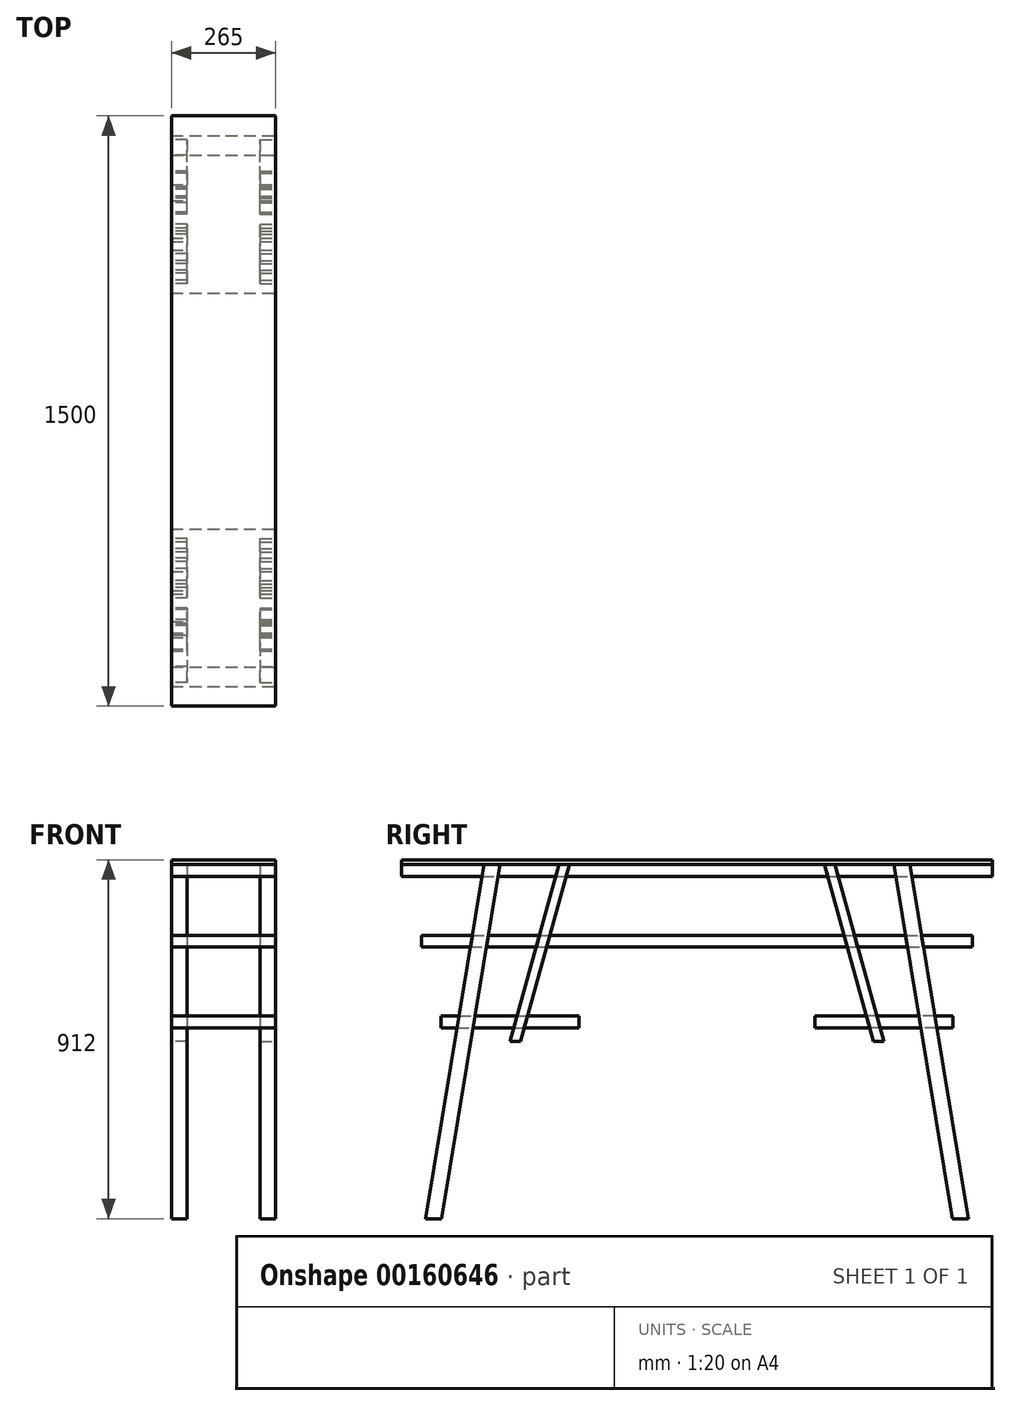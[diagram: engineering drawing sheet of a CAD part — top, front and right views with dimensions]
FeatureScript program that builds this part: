
annotation { "Feature Type Name" : "Feature", "Feature Type Description" : "" }
export const myFeature = defineFeature(function(context is Context, id is Id, definition is map)
    precondition{}
    {
        {
            var Q0;
            Q0=qCreatedBy(makeId("Right.planeOp"),FACE);
            var sketch = newSketch(context, id + "F0", { "sketchPlane" : qUnion([Q0])});
            skLineSegment(sketch, "E0.bottom", {"start": v(0, 0) * mm, "end": v(1500, 0) * mm, "construction": true});
            skLineSegment(sketch, "E0.top", {"start": v(0, 900) * mm, "end": v(1500, 900) * mm, "construction": true});
            skLineSegment(sketch, "E0.left", {"start": v(0, 0) * mm, "end": v(0, 900) * mm, "construction": true});
            skLineSegment(sketch, "E0.right", {"start": v(1500, 0) * mm, "end": v(1500, 900) * mm, "construction": true});
            skLineSegment(sketch, "E1.bottom", {"start": v(0, 900) * mm, "end": v(1500, 900) * mm});
            skLineSegment(sketch, "E1.top", {"start": v(0, 870) * mm, "end": v(1500, 870) * mm});
            skLineSegment(sketch, "E1.left", {"start": v(0, 900) * mm, "end": v(0, 870) * mm});
            skLineSegment(sketch, "E1.right", {"start": v(1500, 900) * mm, "end": v(1500, 870) * mm});
            skLineSegment(sketch, "E2.bottom", {"start": v(50, 720) * mm, "end": v(1450, 720) * mm});
            skLineSegment(sketch, "E2.top", {"start": v(50, 690) * mm, "end": v(1450, 690) * mm});
            skLineSegment(sketch, "E2.left", {"start": v(50, 720) * mm, "end": v(50, 690) * mm});
            skLineSegment(sketch, "E2.right", {"start": v(1450, 720) * mm, "end": v(1450, 690) * mm});
            skLineSegment(sketch, "E3", {"start": v(250, 900) * mm, "end": v(250, 0) * mm, "construction": true});
            skLineSegment(sketch, "E4", {"start": v(250, 900) * mm, "end": v(100.55, 0) * mm});
            skLineSegment(sketch, "E5", {"start": v(209.45, 900) * mm, "end": v(60, 0) * mm});
            skLineSegment(sketch, "E6", {"start": v(60, 0) * mm, "end": v(100.55, 0) * mm});
            skLineSegment(sketch, "E7.MirrorCS", {"start": v(1250, 900) * mm, "end": v(1399.45, 0) * mm});
            skLineSegment(sketch, "E8.MirrorCS", {"start": v(1290.55, 900) * mm, "end": v(1440, 0) * mm});
            skLineSegment(sketch, "E9.MirrorCS", {"start": v(1440, 0) * mm, "end": v(1399.45, 0) * mm});
            skLineSegment(sketch, "E10", {"start": v(400, 900) * mm, "end": v(275.27, 450) * mm});
            skLineSegment(sketch, "E11", {"start": v(275.27, 450) * mm, "end": v(301.22, 450) * mm});
            skLineSegment(sketch, "E12", {"start": v(301.22, 450) * mm, "end": v(425.94, 900) * mm});
            skLineSegment(sketch, "E13.bottom", {"start": v(100, 515) * mm, "end": v(450, 515) * mm});
            skLineSegment(sketch, "E13.top", {"start": v(100, 485) * mm, "end": v(450, 485) * mm});
            skLineSegment(sketch, "E13.left", {"start": v(100, 515) * mm, "end": v(100, 485) * mm});
            skLineSegment(sketch, "E13.right", {"start": v(450, 515) * mm, "end": v(450, 485) * mm});
            skLineSegment(sketch, "E14.MirrorCS", {"start": v(1050, 515) * mm, "end": v(1050, 485) * mm});
            skLineSegment(sketch, "E15.MirrorCS", {"start": v(1400, 515) * mm, "end": v(1400, 485) * mm});
            skLineSegment(sketch, "E16.MirrorCS", {"start": v(1224.73, 450) * mm, "end": v(1198.78, 450) * mm});
            skLineSegment(sketch, "E17.MirrorCS", {"start": v(1400, 515) * mm, "end": v(1050, 515) * mm});
            skLineSegment(sketch, "E18.MirrorCS", {"start": v(1400, 485) * mm, "end": v(1050, 485) * mm});
            skLineSegment(sketch, "E19.MirrorCS", {"start": v(1198.78, 450) * mm, "end": v(1074.06, 900) * mm});
            skLineSegment(sketch, "E20.MirrorCS", {"start": v(1100, 900) * mm, "end": v(1224.73, 450) * mm});
            skLineSegment(sketch, "E21", {"start": v(750, 870) * mm, "end": v(750, 384.96) * mm, "construction": true});
            skPoint(sketch, "E22.orphan", {"position": v(1100, 900) * mm});
            skLineSegment(sketch, "E23", {"start": v(275.27, 450) * mm, "end": v(175.27, 450) * mm, "construction": true});
            skSolve(sketch);
        }
        {
            var Q0;
            {var subQ0=sQuery(id+"F0.wireOp",EDGE,"E1.left");Q0=makeQuery(id+"F0.imprint","IMPRINT",FACE,{"disambiguationData":[TD([[makeQuery(id+"F0.imprint","IMPRINT",EDGE,{"derivedFrom":subQ0}),1.0]])]});}
            var Q1;
            {var subQ0=sQuery(id+"F0.wireOp",EDGE,"E4");var subQ1=sQuery(id+"F0.wireOp",EDGE,"E1.bottom");var subQ2=makeQuery(id+"F0.imprint","INTERSECT",VERTEX,{"derivedFrom":[subQ1,subQ0]});Q1=makeQuery(id+"F0.imprint","IMPRINT",FACE,{"disambiguationData":[TD([[makeQuery(id+"F0.imprint","IMPRINT",EDGE,{"disambiguationData":[TD([[subQ2,1.0]])],"derivedFrom":subQ1}),-1.0]])]});}
            var Q2;
            {var subQ0=sQuery(id+"F0.wireOp",EDGE,"E1.right");Q2=makeQuery(id+"F0.imprint","IMPRINT",FACE,{"disambiguationData":[TD([[makeQuery(id+"F0.imprint","IMPRINT",EDGE,{"derivedFrom":subQ0}),-1.0]])]});}
            var Q3;
            {var subQ0=sQuery(id+"F0.wireOp",EDGE,"E2.left");Q3=makeQuery(id+"F0.imprint","IMPRINT",FACE,{"disambiguationData":[TD([[makeQuery(id+"F0.imprint","IMPRINT",EDGE,{"derivedFrom":subQ0}),1.0]])]});}
            var Q4;
            {var subQ0=sQuery(id+"F0.wireOp",EDGE,"E5");var subQ1=sQuery(id+"F0.wireOp",EDGE,"E2.bottom");var subQ2=makeQuery(id+"F0.imprint","INTERSECT",VERTEX,{"derivedFrom":[subQ1,subQ0]});Q4=makeQuery(id+"F0.imprint","IMPRINT",FACE,{"disambiguationData":[TD([[makeQuery(id+"F0.imprint","IMPRINT",EDGE,{"disambiguationData":[TD([[subQ2,-1.0]])],"derivedFrom":subQ1}),-1.0]])]});}
            var Q5;
            {var subQ0=sQuery(id+"F0.wireOp",EDGE,"E2.right");Q5=makeQuery(id+"F0.imprint","IMPRINT",FACE,{"disambiguationData":[TD([[makeQuery(id+"F0.imprint","IMPRINT",EDGE,{"derivedFrom":subQ0}),-1.0]])]});}
            var Q6;
            {var subQ0=sQuery(id+"F0.wireOp",EDGE,"E4");var subQ1=sQuery(id+"F0.wireOp",EDGE,"E1.bottom");var subQ2=makeQuery(id+"F0.imprint","INTERSECT",VERTEX,{"derivedFrom":[subQ1,subQ0]});Q6=makeQuery(id+"F0.imprint","IMPRINT",FACE,{"disambiguationData":[TD([[makeQuery(id+"F0.imprint","IMPRINT",EDGE,{"disambiguationData":[TD([[subQ2,-1.0]])],"derivedFrom":subQ1}),-1.0]])]});}
            var Q7;
            {var subQ0=sQuery(id+"F0.wireOp",EDGE,"E7.MirrorCS");var subQ1=sQuery(id+"F0.wireOp",EDGE,"E1.bottom");var subQ2=makeQuery(id+"F0.imprint","INTERSECT",VERTEX,{"derivedFrom":[subQ1,subQ0]});Q7=makeQuery(id+"F0.imprint","IMPRINT",FACE,{"disambiguationData":[TD([[makeQuery(id+"F0.imprint","IMPRINT",EDGE,{"disambiguationData":[TD([[subQ2,-1.0]])],"derivedFrom":subQ1}),-1.0]])]});}
            var Q8;
            {var subQ0=sQuery(id+"F0.wireOp",EDGE,"E4");var subQ1=sQuery(id+"F0.wireOp",EDGE,"E2.bottom");var subQ2=makeQuery(id+"F0.imprint","INTERSECT",VERTEX,{"derivedFrom":[subQ1,subQ0]});Q8=makeQuery(id+"F0.imprint","IMPRINT",FACE,{"disambiguationData":[TD([[makeQuery(id+"F0.imprint","IMPRINT",EDGE,{"disambiguationData":[TD([[subQ2,-1.0]])],"derivedFrom":subQ1}),-1.0]])]});}
            var Q9;
            {var subQ0=sQuery(id+"F0.wireOp",EDGE,"E8.MirrorCS");var subQ1=sQuery(id+"F0.wireOp",EDGE,"E2.bottom");var subQ2=makeQuery(id+"F0.imprint","INTERSECT",VERTEX,{"derivedFrom":[subQ1,subQ0]});Q9=makeQuery(id+"F0.imprint","IMPRINT",FACE,{"disambiguationData":[TD([[makeQuery(id+"F0.imprint","IMPRINT",EDGE,{"disambiguationData":[TD([[subQ2,1.0]])],"derivedFrom":subQ1}),-1.0]])]});}
            var Q10;
            {var subQ0=sQuery(id+"F0.wireOp",EDGE,"E10");var subQ1=sQuery(id+"F0.wireOp",EDGE,"E1.bottom");var subQ2=makeQuery(id+"F0.imprint","INTERSECT",VERTEX,{"derivedFrom":[subQ1,subQ0]});Q10=makeQuery(id+"F0.imprint","IMPRINT",FACE,{"disambiguationData":[TD([[makeQuery(id+"F0.imprint","IMPRINT",EDGE,{"disambiguationData":[TD([[subQ2,-1.0]])],"derivedFrom":subQ1}),-1.0]])]});}
            var Q11;
            {var subQ0=sQuery(id+"F0.wireOp",EDGE,"E12");var subQ1=sQuery(id+"F0.wireOp",EDGE,"E1.bottom");var subQ2=makeQuery(id+"F0.imprint","INTERSECT",VERTEX,{"derivedFrom":[subQ1,subQ0]});Q11=makeQuery(id+"F0.imprint","IMPRINT",FACE,{"disambiguationData":[TD([[makeQuery(id+"F0.imprint","IMPRINT",EDGE,{"disambiguationData":[TD([[subQ2,-1.0]])],"derivedFrom":subQ1}),-1.0]])]});}
            var Q12;
            {var subQ0=sQuery(id+"F0.wireOp",EDGE,"E19.MirrorCS");var subQ1=sQuery(id+"F0.wireOp",EDGE,"E1.bottom");var subQ2=makeQuery(id+"F0.imprint","INTERSECT",VERTEX,{"derivedFrom":[subQ1,subQ0]});Q12=makeQuery(id+"F0.imprint","IMPRINT",FACE,{"disambiguationData":[TD([[makeQuery(id+"F0.imprint","IMPRINT",EDGE,{"disambiguationData":[TD([[subQ2,-1.0]])],"derivedFrom":subQ1}),-1.0]])]});}
            var Q13;
            {var subQ0=sQuery(id+"F0.wireOp",EDGE,"E7.MirrorCS");var subQ1=sQuery(id+"F0.wireOp",EDGE,"E1.bottom");var subQ2=makeQuery(id+"F0.imprint","INTERSECT",VERTEX,{"derivedFrom":[subQ1,subQ0]});Q13=makeQuery(id+"F0.imprint","IMPRINT",FACE,{"disambiguationData":[TD([[makeQuery(id+"F0.imprint","IMPRINT",EDGE,{"disambiguationData":[TD([[subQ2,1.0]])],"derivedFrom":subQ1}),-1.0]])]});}
            var Q14;
            {var subQ0=sQuery(id+"F0.wireOp",EDGE,"E10");var subQ1=sQuery(id+"F0.wireOp",EDGE,"E2.bottom");var subQ2=makeQuery(id+"F0.imprint","INTERSECT",VERTEX,{"derivedFrom":[subQ1,subQ0]});Q14=makeQuery(id+"F0.imprint","IMPRINT",FACE,{"disambiguationData":[TD([[makeQuery(id+"F0.imprint","IMPRINT",EDGE,{"disambiguationData":[TD([[subQ2,-1.0]])],"derivedFrom":subQ1}),-1.0]])]});}
            var Q15;
            {var subQ0=sQuery(id+"F0.wireOp",EDGE,"E12");var subQ1=sQuery(id+"F0.wireOp",EDGE,"E2.bottom");var subQ2=makeQuery(id+"F0.imprint","INTERSECT",VERTEX,{"derivedFrom":[subQ1,subQ0]});Q15=makeQuery(id+"F0.imprint","IMPRINT",FACE,{"disambiguationData":[TD([[makeQuery(id+"F0.imprint","IMPRINT",EDGE,{"disambiguationData":[TD([[subQ2,-1.0]])],"derivedFrom":subQ1}),-1.0]])]});}
            var Q16;
            {var subQ0=sQuery(id+"F0.wireOp",EDGE,"E19.MirrorCS");var subQ1=sQuery(id+"F0.wireOp",EDGE,"E2.bottom");var subQ2=makeQuery(id+"F0.imprint","INTERSECT",VERTEX,{"derivedFrom":[subQ1,subQ0]});Q16=makeQuery(id+"F0.imprint","IMPRINT",FACE,{"disambiguationData":[TD([[makeQuery(id+"F0.imprint","IMPRINT",EDGE,{"disambiguationData":[TD([[subQ2,-1.0]])],"derivedFrom":subQ1}),-1.0]])]});}
            var Q17;
            {var subQ0=sQuery(id+"F0.wireOp",EDGE,"E20.MirrorCS");var subQ1=sQuery(id+"F0.wireOp",EDGE,"E2.bottom");var subQ2=makeQuery(id+"F0.imprint","INTERSECT",VERTEX,{"derivedFrom":[subQ1,subQ0]});Q17=makeQuery(id+"F0.imprint","IMPRINT",FACE,{"disambiguationData":[TD([[makeQuery(id+"F0.imprint","IMPRINT",EDGE,{"disambiguationData":[TD([[subQ2,-1.0]])],"derivedFrom":subQ1}),-1.0]])]});}
            var Q18;
            {var subQ5=sQuery(id+"F0.wireOp",EDGE,"E13.left");Q18=makeQuery(id+"F0.imprint","IMPRINT",FACE,{"disambiguationData":[TD([[makeQuery(id+"F0.imprint","IMPRINT",EDGE,{"derivedFrom":subQ5}),1.0]])]});}
            var Q19;
            {var subQ0=sQuery(id+"F0.wireOp",EDGE,"E13.top");var subQ1=sQuery(id+"F0.wireOp",EDGE,"E4");var subQ2=makeQuery(id+"F0.imprint","INTERSECT",VERTEX,{"derivedFrom":[subQ1,subQ0]});Q19=makeQuery(id+"F0.imprint","IMPRINT",FACE,{"disambiguationData":[TD([[makeQuery(id+"F0.imprint","IMPRINT",EDGE,{"disambiguationData":[TD([[subQ2,1.0]])],"derivedFrom":subQ1}),-1.0]])]});}
            var Q20;
            {var subQ0=sQuery(id+"F0.wireOp",EDGE,"E13.top");var subQ1=sQuery(id+"F0.wireOp",EDGE,"E4");var subQ2=makeQuery(id+"F0.imprint","INTERSECT",VERTEX,{"derivedFrom":[subQ1,subQ0]});Q20=makeQuery(id+"F0.imprint","IMPRINT",FACE,{"disambiguationData":[TD([[makeQuery(id+"F0.imprint","IMPRINT",EDGE,{"disambiguationData":[TD([[subQ2,1.0]])],"derivedFrom":subQ1}),1.0]])]});}
            var Q21;
            {var subQ0=sQuery(id+"F0.wireOp",EDGE,"E13.top");var subQ1=sQuery(id+"F0.wireOp",EDGE,"E10");var subQ2=makeQuery(id+"F0.imprint","INTERSECT",VERTEX,{"derivedFrom":[subQ1,subQ0]});Q21=makeQuery(id+"F0.imprint","IMPRINT",FACE,{"disambiguationData":[TD([[makeQuery(id+"F0.imprint","IMPRINT",EDGE,{"disambiguationData":[TD([[subQ2,1.0]])],"derivedFrom":subQ1}),1.0]])]});}
            var Q22;
            {var subQ5=sQuery(id+"F0.wireOp",EDGE,"E13.right");Q22=makeQuery(id+"F0.imprint","IMPRINT",FACE,{"disambiguationData":[TD([[makeQuery(id+"F0.imprint","IMPRINT",EDGE,{"derivedFrom":subQ5}),-1.0]])]});}
            var Q23;
            {var subQ0=sQuery(id+"F0.wireOp",EDGE,"E14.MirrorCS");Q23=makeQuery(id+"F0.imprint","IMPRINT",FACE,{"disambiguationData":[TD([[makeQuery(id+"F0.imprint","IMPRINT",EDGE,{"derivedFrom":subQ0}),1.0]])]});}
            var Q24;
            {var subQ0=sQuery(id+"F0.wireOp",EDGE,"E19.MirrorCS");var subQ1=sQuery(id+"F0.wireOp",EDGE,"E17.MirrorCS");var subQ2=makeQuery(id+"F0.imprint","INTERSECT",VERTEX,{"derivedFrom":[subQ1,subQ0]});Q24=makeQuery(id+"F0.imprint","IMPRINT",FACE,{"disambiguationData":[TD([[makeQuery(id+"F0.imprint","IMPRINT",EDGE,{"disambiguationData":[TD([[subQ2,1.0]])],"derivedFrom":subQ1}),1.0]])]});}
            var Q25;
            {var subQ0=sQuery(id+"F0.wireOp",EDGE,"E18.MirrorCS");var subQ1=sQuery(id+"F0.wireOp",EDGE,"E7.MirrorCS");var subQ2=makeQuery(id+"F0.imprint","INTERSECT",VERTEX,{"derivedFrom":[subQ1,subQ0]});Q25=makeQuery(id+"F0.imprint","IMPRINT",FACE,{"disambiguationData":[TD([[makeQuery(id+"F0.imprint","IMPRINT",EDGE,{"disambiguationData":[TD([[subQ2,1.0]])],"derivedFrom":subQ1}),-1.0]])]});}
            var Q26;
            {var subQ0=sQuery(id+"F0.wireOp",EDGE,"E18.MirrorCS");var subQ1=sQuery(id+"F0.wireOp",EDGE,"E7.MirrorCS");var subQ2=makeQuery(id+"F0.imprint","INTERSECT",VERTEX,{"derivedFrom":[subQ1,subQ0]});Q26=makeQuery(id+"F0.imprint","IMPRINT",FACE,{"disambiguationData":[TD([[makeQuery(id+"F0.imprint","IMPRINT",EDGE,{"disambiguationData":[TD([[subQ2,1.0]])],"derivedFrom":subQ1}),1.0]])]});}
            var Q27;
            {var subQ5=sQuery(id+"F0.wireOp",EDGE,"E15.MirrorCS");Q27=makeQuery(id+"F0.imprint","IMPRINT",FACE,{"disambiguationData":[TD([[makeQuery(id+"F0.imprint","IMPRINT",EDGE,{"derivedFrom":subQ5}),-1.0]])]});}
            extrude(context, id + "F1", {"entities" : qUnion([Q0, Q1, Q2, Q3, Q4, Q5, Q6, Q7, Q8, Q9, Q10, Q11, Q12, Q13, Q14, Q15, Q16, Q17, Q18, Q19, Q20, Q21, Q22, Q23, Q24, Q25, Q26, Q27]), "oppositeDirection" : true, "depth" : 265 * mm});
        }
        {
            var Q0;
            Q0=makeQuery(id+"F1.opExtrude","CAP_FACE",FACE,{"disambiguationData":[OSD([sQuery(id+"F0.wireOp",EDGE,"E1.bottom"),sQuery(id+"F0.wireOp",EDGE,"E1.top"),sQuery(id+"F0.wireOp",EDGE,"E1.left"),sQuery(id+"F0.wireOp",EDGE,"E1.right")])],"isStart":false});
            var sketch = newSketch(context, id + "F2", { "sketchPlane" : qUnion([Q0])});
            skLineSegment(sketch, "E24.0", {"start": v(-209.45, 900) * mm, "end": v(-60, 0) * mm});
            skLineSegment(sketch, "E25.0", {"start": v(-250, 900) * mm, "end": v(-100.55, 0) * mm});
            skLineSegment(sketch, "E26.0", {"start": v(-1250, 900) * mm, "end": v(-1399.45, 0) * mm});
            skLineSegment(sketch, "E27.0", {"start": v(-1290.55, 900) * mm, "end": v(-1440, 0) * mm});
            skLineSegment(sketch, "E28.0", {"start": v(-1440, 0) * mm, "end": v(-1399.45, 0) * mm});
            skLineSegment(sketch, "E29.0", {"start": v(-60, 0) * mm, "end": v(-100.55, 0) * mm});
            skLineSegment(sketch, "E30.0", {"start": v(0, 900) * mm, "end": v(-1500, 900) * mm});
            skLineSegment(sketch, "E31.0", {"start": v(-301.22, 450) * mm, "end": v(-425.94, 900) * mm});
            skLineSegment(sketch, "E32.0", {"start": v(-275.27, 450) * mm, "end": v(-301.22, 450) * mm});
            skLineSegment(sketch, "E33.0", {"start": v(-400, 900) * mm, "end": v(-275.27, 450) * mm});
            skLineSegment(sketch, "E34.0", {"start": v(-1100, 900) * mm, "end": v(-1224.73, 450) * mm});
            skLineSegment(sketch, "E34.1", {"start": v(-1198.78, 450) * mm, "end": v(-1074.06, 900) * mm});
            skLineSegment(sketch, "E34.2", {"start": v(-1224.73, 450) * mm, "end": v(-1198.78, 450) * mm});
            skLineSegment(sketch, "E35.0", {"start": v(-100, 515) * mm, "end": v(-450, 515) * mm});
            skLineSegment(sketch, "E36.0", {"start": v(-50, 720) * mm, "end": v(-1450, 720) * mm});
            skSolve(sketch);
        }
        {
            var Q0;
            {var subQ0=sQuery(id+"F0.wireOp",EDGE,"E4");var subQ1=sQuery(id+"F0.wireOp",EDGE,"E1.bottom");var subQ2=makeQuery(id+"F0.imprint","INTERSECT",VERTEX,{"derivedFrom":[subQ1,subQ0]});Q0=makeQuery(id+"F0.imprint","IMPRINT",FACE,{"disambiguationData":[TD([[makeQuery(id+"F0.imprint","IMPRINT",EDGE,{"disambiguationData":[TD([[subQ2,1.0]])],"derivedFrom":subQ1}),-1.0]])]});}
            var Q1;
            {var subQ0=sQuery(id+"F0.wireOp",EDGE,"E5");var subQ1=sQuery(id+"F0.wireOp",EDGE,"E2.bottom");var subQ2=makeQuery(id+"F0.imprint","INTERSECT",VERTEX,{"derivedFrom":[subQ1,subQ0]});Q1=makeQuery(id+"F0.imprint","IMPRINT",FACE,{"disambiguationData":[TD([[makeQuery(id+"F0.imprint","IMPRINT",EDGE,{"disambiguationData":[TD([[subQ2,-1.0]])],"derivedFrom":subQ1}),-1.0]])]});}
            var Q2;
            {var subQ0=sQuery(id+"F0.wireOp",EDGE,"E7.MirrorCS");var subQ1=sQuery(id+"F0.wireOp",EDGE,"E1.bottom");var subQ2=makeQuery(id+"F0.imprint","INTERSECT",VERTEX,{"derivedFrom":[subQ1,subQ0]});Q2=makeQuery(id+"F0.imprint","IMPRINT",FACE,{"disambiguationData":[TD([[makeQuery(id+"F0.imprint","IMPRINT",EDGE,{"disambiguationData":[TD([[subQ2,-1.0]])],"derivedFrom":subQ1}),-1.0]])]});}
            var Q3;
            {var subQ0=sQuery(id+"F0.wireOp",EDGE,"E8.MirrorCS");var subQ1=sQuery(id+"F0.wireOp",EDGE,"E2.bottom");var subQ2=makeQuery(id+"F0.imprint","INTERSECT",VERTEX,{"derivedFrom":[subQ1,subQ0]});Q3=makeQuery(id+"F0.imprint","IMPRINT",FACE,{"disambiguationData":[TD([[makeQuery(id+"F0.imprint","IMPRINT",EDGE,{"disambiguationData":[TD([[subQ2,1.0]])],"derivedFrom":subQ1}),-1.0]])]});}
            var Q4;
            {var subQ0=sQuery(id+"F0.wireOp",EDGE,"E10");var subQ1=sQuery(id+"F0.wireOp",EDGE,"E2.bottom");var subQ2=makeQuery(id+"F0.imprint","INTERSECT",VERTEX,{"derivedFrom":[subQ1,subQ0]});Q4=makeQuery(id+"F0.imprint","IMPRINT",FACE,{"disambiguationData":[TD([[makeQuery(id+"F0.imprint","IMPRINT",EDGE,{"disambiguationData":[TD([[subQ2,-1.0]])],"derivedFrom":subQ1}),-1.0]])]});}
            var Q5;
            {var subQ0=sQuery(id+"F0.wireOp",EDGE,"E10");var subQ1=sQuery(id+"F0.wireOp",EDGE,"E1.bottom");var subQ2=makeQuery(id+"F0.imprint","INTERSECT",VERTEX,{"derivedFrom":[subQ1,subQ0]});Q5=makeQuery(id+"F0.imprint","IMPRINT",FACE,{"disambiguationData":[TD([[makeQuery(id+"F0.imprint","IMPRINT",EDGE,{"disambiguationData":[TD([[subQ2,-1.0]])],"derivedFrom":subQ1}),-1.0]])]});}
            var Q6;
            {var subQ0=sQuery(id+"F0.wireOp",EDGE,"E19.MirrorCS");var subQ1=sQuery(id+"F0.wireOp",EDGE,"E1.bottom");var subQ2=makeQuery(id+"F0.imprint","INTERSECT",VERTEX,{"derivedFrom":[subQ1,subQ0]});Q6=makeQuery(id+"F0.imprint","IMPRINT",FACE,{"disambiguationData":[TD([[makeQuery(id+"F0.imprint","IMPRINT",EDGE,{"disambiguationData":[TD([[subQ2,-1.0]])],"derivedFrom":subQ1}),-1.0]])]});}
            var Q7;
            {var subQ0=sQuery(id+"F0.wireOp",EDGE,"E19.MirrorCS");var subQ1=sQuery(id+"F0.wireOp",EDGE,"E2.bottom");var subQ2=makeQuery(id+"F0.imprint","INTERSECT",VERTEX,{"derivedFrom":[subQ1,subQ0]});Q7=makeQuery(id+"F0.imprint","IMPRINT",FACE,{"disambiguationData":[TD([[makeQuery(id+"F0.imprint","IMPRINT",EDGE,{"disambiguationData":[TD([[subQ2,-1.0]])],"derivedFrom":subQ1}),-1.0]])]});}
            var Q8;
            {var subQ0=sQuery(id+"F0.wireOp",EDGE,"E13.top");var subQ1=sQuery(id+"F0.wireOp",EDGE,"E4");var subQ2=makeQuery(id+"F0.imprint","INTERSECT",VERTEX,{"derivedFrom":[subQ1,subQ0]});Q8=makeQuery(id+"F0.imprint","IMPRINT",FACE,{"disambiguationData":[TD([[makeQuery(id+"F0.imprint","IMPRINT",EDGE,{"disambiguationData":[TD([[subQ2,1.0]])],"derivedFrom":subQ1}),-1.0]])]});}
            var Q9;
            {var subQ0=sQuery(id+"F0.wireOp",EDGE,"E13.top");var subQ1=sQuery(id+"F0.wireOp",EDGE,"E10");var subQ2=makeQuery(id+"F0.imprint","INTERSECT",VERTEX,{"derivedFrom":[subQ1,subQ0]});Q9=makeQuery(id+"F0.imprint","IMPRINT",FACE,{"disambiguationData":[TD([[makeQuery(id+"F0.imprint","IMPRINT",EDGE,{"disambiguationData":[TD([[subQ2,1.0]])],"derivedFrom":subQ1}),1.0]])]});}
            var Q10;
            {var subQ0=sQuery(id+"F0.wireOp",EDGE,"E19.MirrorCS");var subQ1=sQuery(id+"F0.wireOp",EDGE,"E17.MirrorCS");var subQ2=makeQuery(id+"F0.imprint","INTERSECT",VERTEX,{"derivedFrom":[subQ1,subQ0]});Q10=makeQuery(id+"F0.imprint","IMPRINT",FACE,{"disambiguationData":[TD([[makeQuery(id+"F0.imprint","IMPRINT",EDGE,{"disambiguationData":[TD([[subQ2,1.0]])],"derivedFrom":subQ1}),1.0]])]});}
            var Q11;
            {var subQ0=sQuery(id+"F0.wireOp",EDGE,"E18.MirrorCS");var subQ1=sQuery(id+"F0.wireOp",EDGE,"E7.MirrorCS");var subQ2=makeQuery(id+"F0.imprint","INTERSECT",VERTEX,{"derivedFrom":[subQ1,subQ0]});Q11=makeQuery(id+"F0.imprint","IMPRINT",FACE,{"disambiguationData":[TD([[makeQuery(id+"F0.imprint","IMPRINT",EDGE,{"disambiguationData":[TD([[subQ2,1.0]])],"derivedFrom":subQ1}),1.0]])]});}
            extrude(context, id + "F3", {"entities" : qUnion([Q0, Q1, Q2, Q3, Q4, Q5, Q6, Q7, Q8, Q9, Q10, Q11]), "operationType" : NewBodyOperationType.REMOVE, "oppositeDirection" : true, "depth" : 40 * mm});
        }
        {
            var Q0;
            {var subQ0=sQuery(id+"F2.wireOp",EDGE,"E30.0");var subQ1=sQuery(id+"F2.wireOp",EDGE,"E26.0");var subQ2=makeQuery(id+"F2.imprint","INTERSECT",VERTEX,{"derivedFrom":[subQ1,subQ0]});Q0=makeQuery(id+"F2.imprint","IMPRINT",FACE,{"disambiguationData":[TD([[makeQuery(id+"F2.imprint","IMPRINT",EDGE,{"disambiguationData":[TD([[subQ2,-1.0]])],"derivedFrom":subQ1}),-1.0]])]});}
            var Q1;
            {var subQ0=sQuery(id+"F2.wireOp",EDGE,"E30.0");var subQ1=sQuery(id+"F2.wireOp",EDGE,"E34.0");var subQ2=makeQuery(id+"F2.imprint","INTERSECT",VERTEX,{"derivedFrom":[subQ1,subQ0]});Q1=makeQuery(id+"F2.imprint","IMPRINT",FACE,{"disambiguationData":[TD([[makeQuery(id+"F2.imprint","IMPRINT",EDGE,{"disambiguationData":[TD([[subQ2,-1.0]])],"derivedFrom":subQ1}),1.0]])]});}
            var Q2;
            {var subQ0=sQuery(id+"F2.wireOp",EDGE,"E30.0");var subQ1=sQuery(id+"F2.wireOp",EDGE,"E31.0");var subQ2=makeQuery(id+"F2.imprint","INTERSECT",VERTEX,{"derivedFrom":[subQ1,subQ0]});Q2=makeQuery(id+"F2.imprint","IMPRINT",FACE,{"disambiguationData":[TD([[makeQuery(id+"F2.imprint","IMPRINT",EDGE,{"disambiguationData":[TD([[subQ2,1.0]])],"derivedFrom":subQ1}),-1.0]])]});}
            var Q3;
            {var subQ0=sQuery(id+"F2.wireOp",EDGE,"E30.0");var subQ1=sQuery(id+"F2.wireOp",EDGE,"E24.0");var subQ2=makeQuery(id+"F2.imprint","INTERSECT",VERTEX,{"derivedFrom":[subQ1,subQ0]});Q3=makeQuery(id+"F2.imprint","IMPRINT",FACE,{"disambiguationData":[TD([[makeQuery(id+"F2.imprint","IMPRINT",EDGE,{"disambiguationData":[TD([[subQ2,-1.0]])],"derivedFrom":subQ1}),-1.0]])]});}
            var Q4;
            {var subQ0=sQuery(id+"F2.wireOp",EDGE,"E28.0");Q4=makeQuery(id+"F2.imprint","IMPRINT",FACE,{"disambiguationData":[TD([[makeQuery(id+"F2.imprint","IMPRINT",EDGE,{"derivedFrom":subQ0}),1.0]])]});}
            var Q5;
            {var subQ0=sQuery(id+"F2.wireOp",EDGE,"E34.2");Q5=makeQuery(id+"F2.imprint","IMPRINT",FACE,{"disambiguationData":[TD([[makeQuery(id+"F2.imprint","IMPRINT",EDGE,{"derivedFrom":subQ0}),1.0]])]});}
            var Q6;
            {var subQ0=sQuery(id+"F2.wireOp",EDGE,"E35.0");var subQ1=sQuery(id+"F2.wireOp",EDGE,"E31.0");var subQ2=makeQuery(id+"F2.imprint","INTERSECT",VERTEX,{"derivedFrom":[subQ1,subQ0]});Q6=makeQuery(id+"F2.imprint","IMPRINT",FACE,{"disambiguationData":[TD([[makeQuery(id+"F2.imprint","IMPRINT",EDGE,{"disambiguationData":[TD([[subQ2,-1.0]])],"derivedFrom":subQ1}),-1.0]])]});}
            var Q7;
            {var subQ0=sQuery(id+"F2.wireOp",EDGE,"E32.0");Q7=makeQuery(id+"F2.imprint","IMPRINT",FACE,{"disambiguationData":[TD([[makeQuery(id+"F2.imprint","IMPRINT",EDGE,{"derivedFrom":subQ0}),-1.0]])]});}
            var Q8;
            {var subQ0=sQuery(id+"F2.wireOp",EDGE,"E36.0");var subQ1=sQuery(id+"F2.wireOp",EDGE,"E24.0");var subQ2=makeQuery(id+"F2.imprint","INTERSECT",VERTEX,{"derivedFrom":[subQ1,subQ0]});Q8=makeQuery(id+"F2.imprint","IMPRINT",FACE,{"disambiguationData":[TD([[makeQuery(id+"F2.imprint","IMPRINT",EDGE,{"disambiguationData":[TD([[subQ2,-1.0]])],"derivedFrom":subQ1}),-1.0]])]});}
            var Q9;
            {var subQ0=sQuery(id+"F2.wireOp",EDGE,"E29.0");Q9=makeQuery(id+"F2.imprint","IMPRINT",FACE,{"disambiguationData":[TD([[makeQuery(id+"F2.imprint","IMPRINT",EDGE,{"derivedFrom":subQ0}),-1.0]])]});}
            extrude(context, id + "F4", {"entities" : qUnion([Q0, Q1, Q2, Q3, Q4, Q5, Q6, Q7, Q8, Q9]), "operationType" : NewBodyOperationType.REMOVE, "oppositeDirection" : true, "depth" : 40 * mm});
        }
        {
            var Q0;
            {var subQ0=sQuery(id+"F0.wireOp",EDGE,"E4");var subQ1=sQuery(id+"F0.wireOp",EDGE,"E1.bottom");var subQ2=makeQuery(id+"F0.imprint","INTERSECT",VERTEX,{"derivedFrom":[subQ1,subQ0]});Q0=makeQuery(id+"F0.imprint","IMPRINT",FACE,{"disambiguationData":[TD([[makeQuery(id+"F0.imprint","IMPRINT",EDGE,{"disambiguationData":[TD([[subQ2,1.0]])],"derivedFrom":subQ1}),-1.0]])]});}
            var Q1;
            {var subQ0=sQuery(id+"F0.wireOp",EDGE,"E5");var subQ1=sQuery(id+"F0.wireOp",EDGE,"E1.top");var subQ2=makeQuery(id+"F0.imprint","INTERSECT",VERTEX,{"derivedFrom":[subQ1,subQ0]});Q1=makeQuery(id+"F0.imprint","IMPRINT",FACE,{"disambiguationData":[TD([[makeQuery(id+"F0.imprint","IMPRINT",EDGE,{"disambiguationData":[TD([[subQ2,-1.0]])],"derivedFrom":subQ1}),-1.0]])]});}
            var Q2;
            {var subQ5=sQuery(id+"F0.wireOp",EDGE,"E6");Q2=makeQuery(id+"F0.imprint","IMPRINT",FACE,{"disambiguationData":[TD([[makeQuery(id+"F0.imprint","IMPRINT",EDGE,{"derivedFrom":subQ5}),1.0]])]});}
            var Q3;
            {var subQ0=sQuery(id+"F0.wireOp",EDGE,"E7.MirrorCS");var subQ1=sQuery(id+"F0.wireOp",EDGE,"E1.bottom");var subQ2=makeQuery(id+"F0.imprint","INTERSECT",VERTEX,{"derivedFrom":[subQ1,subQ0]});Q3=makeQuery(id+"F0.imprint","IMPRINT",FACE,{"disambiguationData":[TD([[makeQuery(id+"F0.imprint","IMPRINT",EDGE,{"disambiguationData":[TD([[subQ2,-1.0]])],"derivedFrom":subQ1}),-1.0]])]});}
            var Q4;
            {var subQ0=sQuery(id+"F0.wireOp",EDGE,"E8.MirrorCS");var subQ1=sQuery(id+"F0.wireOp",EDGE,"E1.top");var subQ2=makeQuery(id+"F0.imprint","INTERSECT",VERTEX,{"derivedFrom":[subQ1,subQ0]});Q4=makeQuery(id+"F0.imprint","IMPRINT",FACE,{"disambiguationData":[TD([[makeQuery(id+"F0.imprint","IMPRINT",EDGE,{"disambiguationData":[TD([[subQ2,1.0]])],"derivedFrom":subQ1}),-1.0]])]});}
            var Q5;
            {var subQ0=sQuery(id+"F0.wireOp",EDGE,"E8.MirrorCS");var subQ1=sQuery(id+"F0.wireOp",EDGE,"E2.bottom");var subQ2=makeQuery(id+"F0.imprint","INTERSECT",VERTEX,{"derivedFrom":[subQ1,subQ0]});Q5=makeQuery(id+"F0.imprint","IMPRINT",FACE,{"disambiguationData":[TD([[makeQuery(id+"F0.imprint","IMPRINT",EDGE,{"disambiguationData":[TD([[subQ2,1.0]])],"derivedFrom":subQ1}),-1.0]])]});}
            var Q6;
            {var subQ5=sQuery(id+"F0.wireOp",EDGE,"E9.MirrorCS");Q6=makeQuery(id+"F0.imprint","IMPRINT",FACE,{"disambiguationData":[TD([[makeQuery(id+"F0.imprint","IMPRINT",EDGE,{"derivedFrom":subQ5}),-1.0]])]});}
            var Q7;
            {var subQ0=sQuery(id+"F0.wireOp",EDGE,"E5");var subQ1=sQuery(id+"F0.wireOp",EDGE,"E2.top");var subQ2=makeQuery(id+"F0.imprint","INTERSECT",VERTEX,{"derivedFrom":[subQ1,subQ0]});Q7=makeQuery(id+"F0.imprint","IMPRINT",FACE,{"disambiguationData":[TD([[makeQuery(id+"F0.imprint","IMPRINT",EDGE,{"disambiguationData":[TD([[subQ2,-1.0]])],"derivedFrom":subQ1}),-1.0]])]});}
            var Q8;
            {var subQ0=sQuery(id+"F0.wireOp",EDGE,"E5");var subQ1=sQuery(id+"F0.wireOp",EDGE,"E2.bottom");var subQ2=makeQuery(id+"F0.imprint","INTERSECT",VERTEX,{"derivedFrom":[subQ1,subQ0]});Q8=makeQuery(id+"F0.imprint","IMPRINT",FACE,{"disambiguationData":[TD([[makeQuery(id+"F0.imprint","IMPRINT",EDGE,{"disambiguationData":[TD([[subQ2,-1.0]])],"derivedFrom":subQ1}),-1.0]])]});}
            var Q9;
            {var subQ0=sQuery(id+"F0.wireOp",EDGE,"E13.top");var subQ1=sQuery(id+"F0.wireOp",EDGE,"E4");var subQ2=makeQuery(id+"F0.imprint","INTERSECT",VERTEX,{"derivedFrom":[subQ1,subQ0]});Q9=makeQuery(id+"F0.imprint","IMPRINT",FACE,{"disambiguationData":[TD([[makeQuery(id+"F0.imprint","IMPRINT",EDGE,{"disambiguationData":[TD([[subQ2,1.0]])],"derivedFrom":subQ1}),-1.0]])]});}
            var Q10;
            {var subQ0=sQuery(id+"F0.wireOp",EDGE,"E8.MirrorCS");var subQ1=sQuery(id+"F0.wireOp",EDGE,"E2.top");var subQ2=makeQuery(id+"F0.imprint","INTERSECT",VERTEX,{"derivedFrom":[subQ1,subQ0]});Q10=makeQuery(id+"F0.imprint","IMPRINT",FACE,{"disambiguationData":[TD([[makeQuery(id+"F0.imprint","IMPRINT",EDGE,{"disambiguationData":[TD([[subQ2,1.0]])],"derivedFrom":subQ1}),-1.0]])]});}
            var Q11;
            {var subQ0=sQuery(id+"F0.wireOp",EDGE,"E18.MirrorCS");var subQ1=sQuery(id+"F0.wireOp",EDGE,"E7.MirrorCS");var subQ2=makeQuery(id+"F0.imprint","INTERSECT",VERTEX,{"derivedFrom":[subQ1,subQ0]});Q11=makeQuery(id+"F0.imprint","IMPRINT",FACE,{"disambiguationData":[TD([[makeQuery(id+"F0.imprint","IMPRINT",EDGE,{"disambiguationData":[TD([[subQ2,1.0]])],"derivedFrom":subQ1}),1.0]])]});}
            var Q12;
            {var subQ0=sQuery(id+"F0.wireOp",EDGE,"E10");var subQ1=sQuery(id+"F0.wireOp",EDGE,"E1.bottom");var subQ2=makeQuery(id+"F0.imprint","INTERSECT",VERTEX,{"derivedFrom":[subQ1,subQ0]});Q12=makeQuery(id+"F0.imprint","IMPRINT",FACE,{"disambiguationData":[TD([[makeQuery(id+"F0.imprint","IMPRINT",EDGE,{"disambiguationData":[TD([[subQ2,-1.0]])],"derivedFrom":subQ1}),-1.0]])]});}
            var Q13;
            {var subQ0=sQuery(id+"F0.wireOp",EDGE,"E10");var subQ1=sQuery(id+"F0.wireOp",EDGE,"E1.top");var subQ2=makeQuery(id+"F0.imprint","INTERSECT",VERTEX,{"derivedFrom":[subQ1,subQ0]});Q13=makeQuery(id+"F0.imprint","IMPRINT",FACE,{"disambiguationData":[TD([[makeQuery(id+"F0.imprint","IMPRINT",EDGE,{"disambiguationData":[TD([[subQ2,-1.0]])],"derivedFrom":subQ1}),-1.0]])]});}
            var Q14;
            {var subQ0=sQuery(id+"F0.wireOp",EDGE,"E10");var subQ1=sQuery(id+"F0.wireOp",EDGE,"E2.bottom");var subQ2=makeQuery(id+"F0.imprint","INTERSECT",VERTEX,{"derivedFrom":[subQ1,subQ0]});Q14=makeQuery(id+"F0.imprint","IMPRINT",FACE,{"disambiguationData":[TD([[makeQuery(id+"F0.imprint","IMPRINT",EDGE,{"disambiguationData":[TD([[subQ2,-1.0]])],"derivedFrom":subQ1}),-1.0]])]});}
            var Q15;
            {var subQ0=sQuery(id+"F0.wireOp",EDGE,"E12");var subQ1=sQuery(id+"F0.wireOp",EDGE,"E2.top");var subQ2=makeQuery(id+"F0.imprint","INTERSECT",VERTEX,{"derivedFrom":[subQ1,subQ0]});Q15=makeQuery(id+"F0.imprint","IMPRINT",FACE,{"disambiguationData":[TD([[makeQuery(id+"F0.imprint","IMPRINT",EDGE,{"disambiguationData":[TD([[subQ2,1.0]])],"derivedFrom":subQ1}),-1.0]])]});}
            var Q16;
            {var subQ0=sQuery(id+"F0.wireOp",EDGE,"E13.top");var subQ1=sQuery(id+"F0.wireOp",EDGE,"E10");var subQ2=makeQuery(id+"F0.imprint","INTERSECT",VERTEX,{"derivedFrom":[subQ1,subQ0]});Q16=makeQuery(id+"F0.imprint","IMPRINT",FACE,{"disambiguationData":[TD([[makeQuery(id+"F0.imprint","IMPRINT",EDGE,{"disambiguationData":[TD([[subQ2,1.0]])],"derivedFrom":subQ1}),1.0]])]});}
            var Q17;
            {var subQ0=sQuery(id+"F0.wireOp",EDGE,"E11");Q17=makeQuery(id+"F0.imprint","IMPRINT",FACE,{"disambiguationData":[TD([[makeQuery(id+"F0.imprint","IMPRINT",EDGE,{"derivedFrom":subQ0}),1.0]])]});}
            var Q18;
            {var subQ0=sQuery(id+"F0.wireOp",EDGE,"E19.MirrorCS");var subQ1=sQuery(id+"F0.wireOp",EDGE,"E1.bottom");var subQ2=makeQuery(id+"F0.imprint","INTERSECT",VERTEX,{"derivedFrom":[subQ1,subQ0]});Q18=makeQuery(id+"F0.imprint","IMPRINT",FACE,{"disambiguationData":[TD([[makeQuery(id+"F0.imprint","IMPRINT",EDGE,{"disambiguationData":[TD([[subQ2,-1.0]])],"derivedFrom":subQ1}),-1.0]])]});}
            var Q19;
            {var subQ0=sQuery(id+"F0.wireOp",EDGE,"E19.MirrorCS");var subQ1=sQuery(id+"F0.wireOp",EDGE,"E1.top");var subQ2=makeQuery(id+"F0.imprint","INTERSECT",VERTEX,{"derivedFrom":[subQ1,subQ0]});Q19=makeQuery(id+"F0.imprint","IMPRINT",FACE,{"disambiguationData":[TD([[makeQuery(id+"F0.imprint","IMPRINT",EDGE,{"disambiguationData":[TD([[subQ2,-1.0]])],"derivedFrom":subQ1}),-1.0]])]});}
            var Q20;
            {var subQ0=sQuery(id+"F0.wireOp",EDGE,"E19.MirrorCS");var subQ1=sQuery(id+"F0.wireOp",EDGE,"E2.bottom");var subQ2=makeQuery(id+"F0.imprint","INTERSECT",VERTEX,{"derivedFrom":[subQ1,subQ0]});Q20=makeQuery(id+"F0.imprint","IMPRINT",FACE,{"disambiguationData":[TD([[makeQuery(id+"F0.imprint","IMPRINT",EDGE,{"disambiguationData":[TD([[subQ2,-1.0]])],"derivedFrom":subQ1}),-1.0]])]});}
            var Q21;
            {var subQ0=sQuery(id+"F0.wireOp",EDGE,"E19.MirrorCS");var subQ1=sQuery(id+"F0.wireOp",EDGE,"E2.top");var subQ2=makeQuery(id+"F0.imprint","INTERSECT",VERTEX,{"derivedFrom":[subQ1,subQ0]});Q21=makeQuery(id+"F0.imprint","IMPRINT",FACE,{"disambiguationData":[TD([[makeQuery(id+"F0.imprint","IMPRINT",EDGE,{"disambiguationData":[TD([[subQ2,-1.0]])],"derivedFrom":subQ1}),-1.0]])]});}
            var Q22;
            {var subQ0=sQuery(id+"F0.wireOp",EDGE,"E19.MirrorCS");var subQ1=sQuery(id+"F0.wireOp",EDGE,"E17.MirrorCS");var subQ2=makeQuery(id+"F0.imprint","INTERSECT",VERTEX,{"derivedFrom":[subQ1,subQ0]});Q22=makeQuery(id+"F0.imprint","IMPRINT",FACE,{"disambiguationData":[TD([[makeQuery(id+"F0.imprint","IMPRINT",EDGE,{"disambiguationData":[TD([[subQ2,1.0]])],"derivedFrom":subQ1}),1.0]])]});}
            var Q23;
            {var subQ0=sQuery(id+"F0.wireOp",EDGE,"E16.MirrorCS");Q23=makeQuery(id+"F0.imprint","IMPRINT",FACE,{"disambiguationData":[TD([[makeQuery(id+"F0.imprint","IMPRINT",EDGE,{"derivedFrom":subQ0}),-1.0]])]});}
            extrude(context, id + "F5", {"entities" : qUnion([Q0, Q1, Q2, Q3, Q4, Q5, Q6, Q7, Q8, Q9, Q10, Q11, Q12, Q13, Q14, Q15, Q16, Q17, Q18, Q19, Q20, Q21, Q22, Q23]), "oppositeDirection" : true, "depth" : 40 * mm});
        }
        {
            var Q0;
            {var subQ0=sQuery(id+"F0.wireOp",EDGE,"E1.left");Q0=makeQuery(id+"F0.imprint","IMPRINT",FACE,{"disambiguationData":[TD([[makeQuery(id+"F0.imprint","IMPRINT",EDGE,{"derivedFrom":subQ0}),1.0]])]});}
            var Q1;
            {var subQ5=makeQuery(id+"F1.opExtrude","CAP_EDGE",EDGE,{"disambiguationData":[OSD([sQuery(id+"F0.wireOp",EDGE,"E1.left")])],"isStart":false});Q1=makeQuery(id+"F2.imprint","IMPRINT",FACE,{"disambiguationData":[TD([[makeQuery(id+"F2.imprint","IMPRINT",EDGE,{"derivedFrom":subQ5}),-1.0]])]});}
            cPlane(context, id + "F6", {"entities" : qUnion([Q0, Q1]), "cplaneType" : CPlaneType.MID_PLANE, "offset" : 25 * mm, "width" : 150 * mm, "height" : 150 * mm});
        }
        {
            var Q0;
            Q0=makeQuery(id+"F5.opExtrude","SWEPT_BODY",BODY,{"disambiguationData":[OSD([sQuery(id+"F0.wireOp",EDGE,"E1.bottom"),sQuery(id+"F0.wireOp",EDGE,"E4"),sQuery(id+"F0.wireOp",EDGE,"E5"),sQuery(id+"F0.wireOp",EDGE,"E6")])]});
            var Q1;
            Q1=makeQuery(id+"F5.opExtrude","SWEPT_BODY",BODY,{"disambiguationData":[OSD([sQuery(id+"F0.wireOp",EDGE,"E1.bottom"),sQuery(id+"F0.wireOp",EDGE,"E10"),sQuery(id+"F0.wireOp",EDGE,"E11"),sQuery(id+"F0.wireOp",EDGE,"E12")])]});
            var Q2;
            Q2=makeQuery(id+"F5.opExtrude","SWEPT_BODY",BODY,{"disambiguationData":[OSD([sQuery(id+"F0.wireOp",EDGE,"E1.bottom"),sQuery(id+"F0.wireOp",EDGE,"E16.MirrorCS"),sQuery(id+"F0.wireOp",EDGE,"E19.MirrorCS"),sQuery(id+"F0.wireOp",EDGE,"E20.MirrorCS")])]});
            var Q3;
            Q3=makeQuery(id+"F5.opExtrude","SWEPT_BODY",BODY,{"disambiguationData":[OSD([sQuery(id+"F0.wireOp",EDGE,"E1.bottom"),sQuery(id+"F0.wireOp",EDGE,"E7.MirrorCS"),sQuery(id+"F0.wireOp",EDGE,"E8.MirrorCS"),sQuery(id+"F0.wireOp",EDGE,"E9.MirrorCS")])]});
            var Q4;
            Q4=qCreatedBy(id+"F6.planeOp",FACE);
            mirror(context, id + "F7", {"entities" : qUnion([Q0, Q1, Q2, Q3]), "mirrorPlane" : qUnion([Q4])});
        }
        {
            var Q0;
            Q0=makeQuery(id+"F1.opExtrude","SWEPT_FACE",FACE,{"disambiguationData":[OSD([sQuery(id+"F0.wireOp",EDGE,"E1.bottom")])]});
            var sketch = newSketch(context, id + "F8", { "sketchPlane" : qUnion([Q0])});
            skLineSegment(sketch, "E37.bottom", {"start": v(0, 0) * mm, "end": v(-265, 0) * mm});
            skLineSegment(sketch, "E37.top", {"start": v(0, 1500) * mm, "end": v(-265, 1500) * mm});
            skLineSegment(sketch, "E37.left", {"start": v(0, 0) * mm, "end": v(0, 1500) * mm});
            skLineSegment(sketch, "E37.right", {"start": v(-265, 0) * mm, "end": v(-265, 1500) * mm});
            skSolve(sketch);
        }
        {
            var Q0;
            Q0 = qSketchRegion(id + "F8", true);
            extrude(context, id + "F9", {"entities" : qUnion([Q0]), "depth" : 12 * mm});
        }
    });
